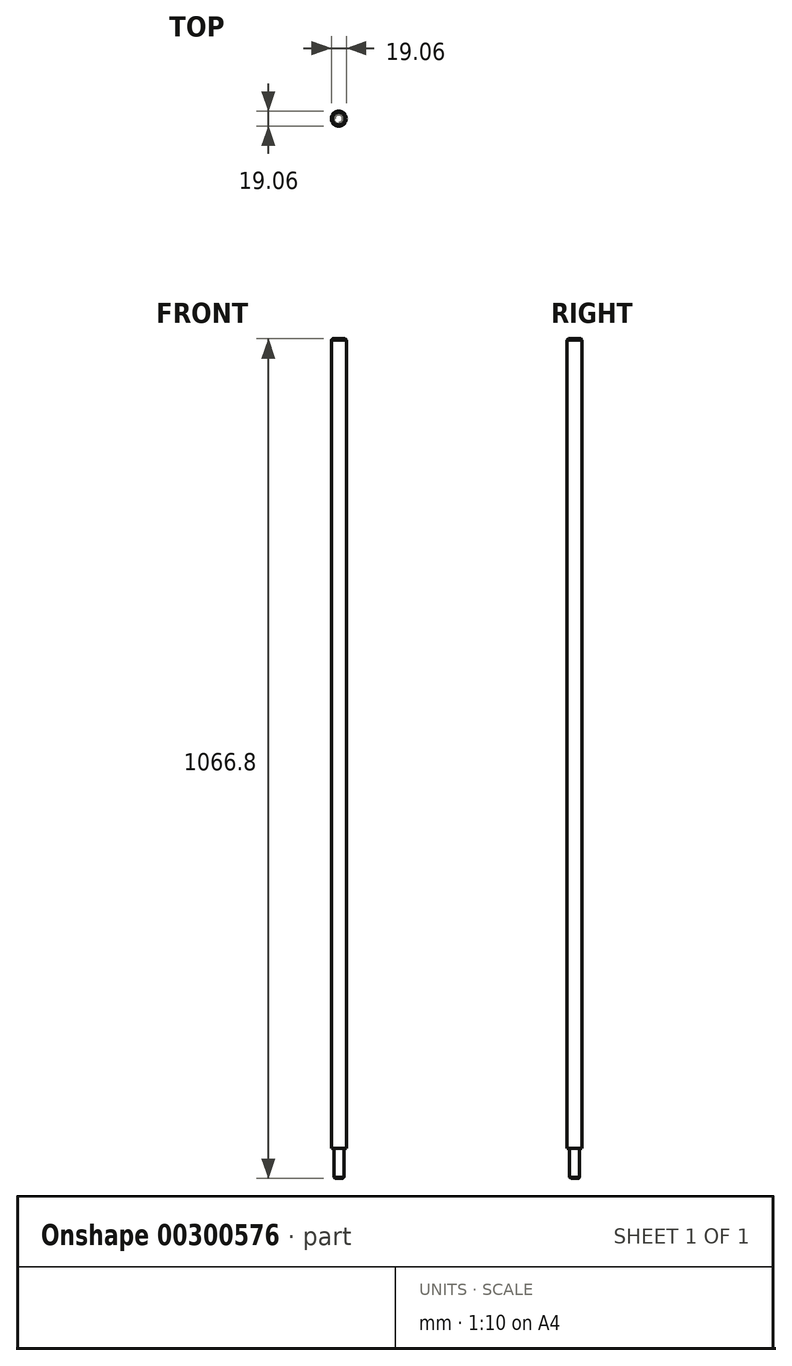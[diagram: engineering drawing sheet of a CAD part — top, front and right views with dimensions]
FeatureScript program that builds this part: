
annotation { "Feature Type Name" : "Feature", "Feature Type Description" : "" }
export const myFeature = defineFeature(function(context is Context, id is Id, definition is map)
    precondition{}
    {
        {
            var Q0;
            Q0=qCreatedBy(makeId("Right.planeOp"),FACE);
            var sketch = newSketch(context, id + "F0", { "sketchPlane" : qUnion([Q0])});
            skLineSegment(sketch, "E0", {"start": v(0, 0) * mm, "end": v(0, 1066.8) * mm});
            skLineSegment(sketch, "E1", {"start": v(0, 1066.8) * mm, "end": v(9.52, 1066.8) * mm});
            skLineSegment(sketch, "E2", {"start": v(9.52, 1066.8) * mm, "end": v(9.52, 38.1) * mm});
            skLineSegment(sketch, "E3", {"start": v(9.52, 38.1) * mm, "end": v(6.35, 38.1) * mm});
            skLineSegment(sketch, "E4", {"start": v(6.35, 38.1) * mm, "end": v(6.35, 0) * mm});
            skLineSegment(sketch, "E5", {"start": v(6.35, 0) * mm, "end": v(0, 0) * mm});
            skSolve(sketch);
        }
        {
            var Q0;
            Q0=makeQuery(id+"F0.imprint","IMPRINT",FACE,{"disambiguationData":[TD([[makeQuery(id+"F0.imprint","IMPRINT",EDGE,{"derivedFrom":sQuery(id+"F0.wireOp",EDGE,"E0")}),-1.0]])]});
            var Q1;
            Q1 = qBodyType(qCreatedBy(id + "F0" ,EDGE), BodyType.WIRE);
            var Q2;
            Q2=sQuery(id+"F0.wireOp",EDGE,"E0");
            revolve(context, id + "F1", {"entities" : qUnion([Q0]), "surfaceEntities" : qUnion([Q1]), "axis" : qUnion([Q2]), "revolveType" : RevolveType.FULL});
        }
        {
            var Q0;
            Q0=makeQuery(id+"F1.opRevolve","SWEPT_EDGE",EDGE,{"disambiguationData":[OSD([sQuery(id+"F0.wireOp",EDGE,"E4"),sQuery(id+"F0.wireOp",EDGE,"E5")])]});
            var Q1;
            Q1=makeQuery(id+"F1.opRevolve","SWEPT_EDGE",EDGE,{"disambiguationData":[OSD([sQuery(id+"F0.wireOp",EDGE,"E1"),sQuery(id+"F0.wireOp",EDGE,"E2")])]});
            chamfer(context, id + "F2", {"entities" : qUnion([Q0, Q1]), "width" : 1.52 * mm, "tangentPropagation" : true});
        }
    });
